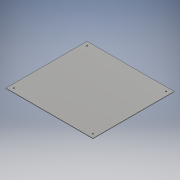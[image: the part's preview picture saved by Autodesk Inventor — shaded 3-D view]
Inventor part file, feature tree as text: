
AUTODESK INVENTOR PART (.ipt)
format: ipt  version: 2018 (Build 220112000, 112)  size: 122,368 bytes
history: native  units: mm
features: sketch x5, hole x4, extrude x1
ambient origin geometry x8: Origin, YZ Plane, XZ Plane, XY Plane, X Axis, Y Axis, Z Axis, Center Point
bodies: Solid1 (feature_tree)
feature tree (10):
  extrude  "Extrusion1"  Depth=411.0mm
  hole  "Hole1"  [1 undecoded]
  hole  "Hole2"  [1 undecoded]
  hole  "Hole3"  [1 undecoded]
  hole  "Hole4"  [1 undecoded]
  sketch  "Sketch1"  dims[d0=383.0mm d1=411.0mm]
  sketch  "Sketch2"  dims[d2=2.0mm d3=0.0mm]
  sketch  "Sketch3"  dims[d7=6.0mm d8=6.0mm d9=4.0mm d10=2.0mm d11=90.0deg d12=8.0mm d13=20.594885mm]
  sketch  "Sketch4"  dims[d17=6.0mm d18=6.0mm d19=4.0mm d20=2.0mm d21=90.0deg d22=8.0mm d23=20.594885mm]
  sketch  "Sketch5"  dims[d27=6.0mm d28=6.0mm d29=4.0mm d30=2.0mm d31=90.0deg d32=8.0mm d33=20.594885mm d37=6.0mm d38=6.0mm d39=4.0mm d40=2.0mm d41=90.0deg d42=8.0mm d43=20.594885mm d44=19.0mm d46=19.0mm d47=6.0mm d49=19.0mm d50=19.0mm d51=6.0mm d53=19.0mm d54=19.0mm d55=6.0mm d56=19.0mm d57=19.0mm d58=6.0mm]
note: 4 required parameter values undecoded (feature->parameter linkage not recoverable at this tier; creation-order binding heuristic only, values carry confidence <= 0.55)
